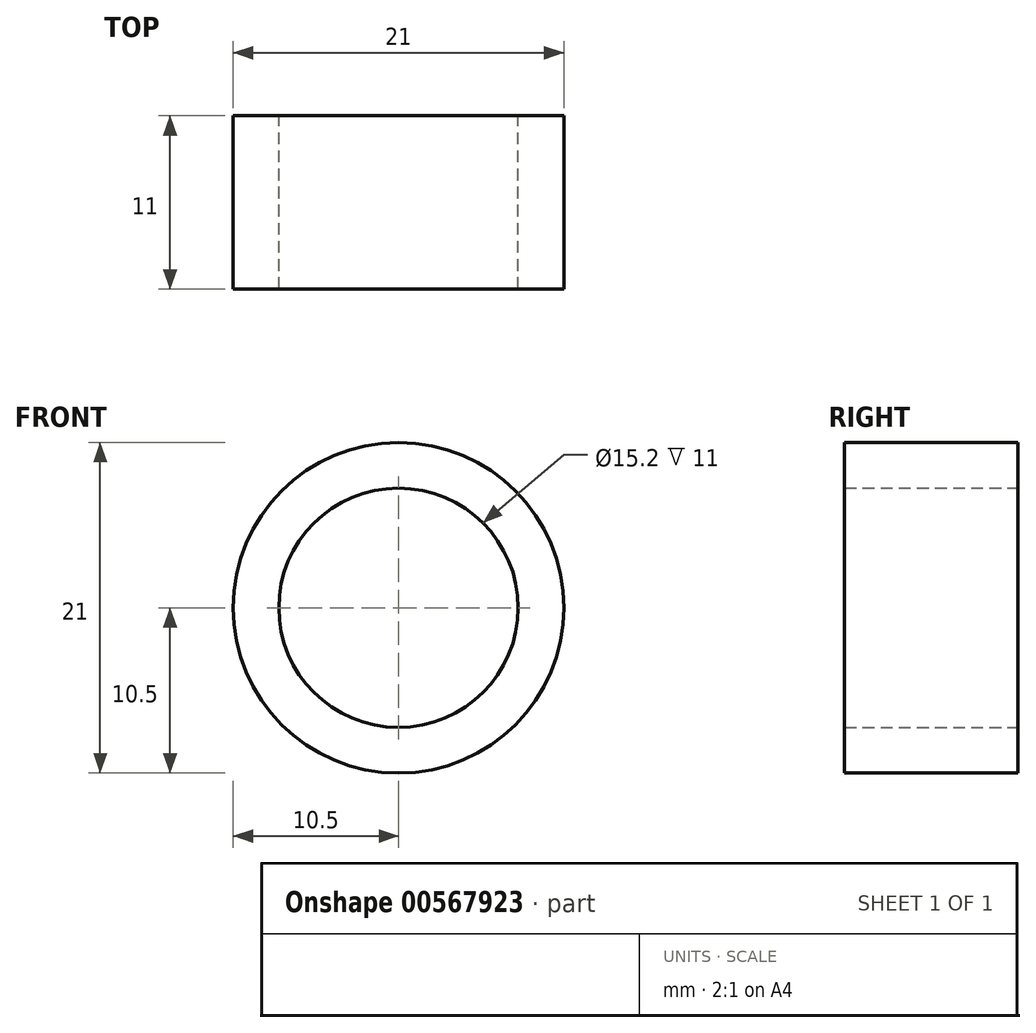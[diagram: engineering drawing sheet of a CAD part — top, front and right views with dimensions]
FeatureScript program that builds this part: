
annotation { "Feature Type Name" : "Feature", "Feature Type Description" : "" }
export const myFeature = defineFeature(function(context is Context, id is Id, definition is map)
    precondition{}
    {
        {
            var Q0;
            Q0=qCreatedBy(makeId("Front.planeOp"),FACE);
            var sketch = newSketch(context, id + "F0", { "sketchPlane" : qUnion([Q0])});
            skCircle(sketch, "E0", {"center": v(0, 0) * mm, "radius": 10.5 * mm});
            skCircle(sketch, "E1", {"center": v(0, 0) * mm, "radius": 7.6 * mm});
            skSolve(sketch);
        }
        {
            var Q0;
            Q0 = qSketchRegion(id + "F0", true);
            extrude(context, id + "F1", {"entities" : qUnion([Q0]), "depth" : 11 * mm, "offsetDistance" : 25 * mm});
        }
    });
